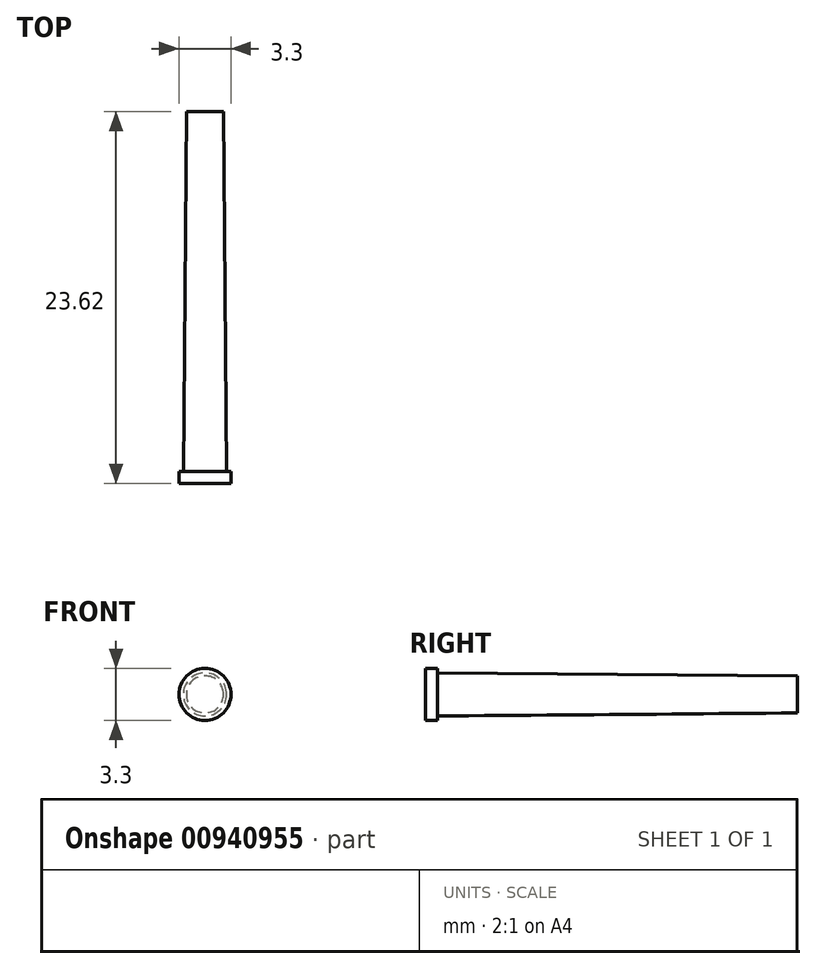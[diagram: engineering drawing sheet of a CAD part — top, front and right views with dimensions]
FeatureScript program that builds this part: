
annotation { "Feature Type Name" : "Feature", "Feature Type Description" : "" }
export const myFeature = defineFeature(function(context is Context, id is Id, definition is map)
    precondition{}
    {
        {
            var Q0;
            Q0=qCreatedBy(makeId("Right.planeOp"),FACE);
            var sketch = newSketch(context, id + "F0", { "sketchPlane" : qUnion([Q0])});
            skLineSegment(sketch, "E0", {"start": v(0, 0) * mm, "end": v(-22.86, 0) * mm});
            skLineSegment(sketch, "E1", {"start": v(-22.86, 0) * mm, "end": v(-23.62, 0) * mm});
            skLineSegment(sketch, "E2", {"start": v(-23.62, 0) * mm, "end": v(-23.62, 1.65) * mm});
            skLineSegment(sketch, "E3", {"start": v(-23.62, 1.65) * mm, "end": v(-22.86, 1.65) * mm});
            skLineSegment(sketch, "E4", {"start": v(0, 1.18) * mm, "end": v(0, 0) * mm});
            skLineSegment(sketch, "E5", {"start": v(-22.86, 1.65) * mm, "end": v(-22.86, 1.37) * mm});
            skLineSegment(sketch, "E6", {"start": v(-22.86, 1.37) * mm, "end": v(0, 1.18) * mm});
            skSolve(sketch);
        }
        {
            var Q0;
            Q0=sQuery(id+"F0.wireOp",EDGE,"E6");
            var Q1;
            Q1=sQuery(id+"F0.wireOp",EDGE,"E2");
            var Q2;
            Q2=sQuery(id+"F0.wireOp",EDGE,"E3");
            var Q3;
            Q3=sQuery(id+"F0.wireOp",EDGE,"E5");
            var Q4;
            Q4=sQuery(id+"F0.wireOp",EDGE,"E4");
            var Q5;
            Q5=sQuery(id+"F0.wireOp",EDGE,"E0");
            revolve(context, id + "F1", {"bodyType" : ToolBodyType.SURFACE, "surfaceOperationType" : NewSurfaceOperationType.NEW, "surfaceEntities" : qUnion([Q0, Q1, Q2, Q3, Q4]), "axis" : qUnion([Q5]), "revolveType" : RevolveType.FULL});
        }
    });
